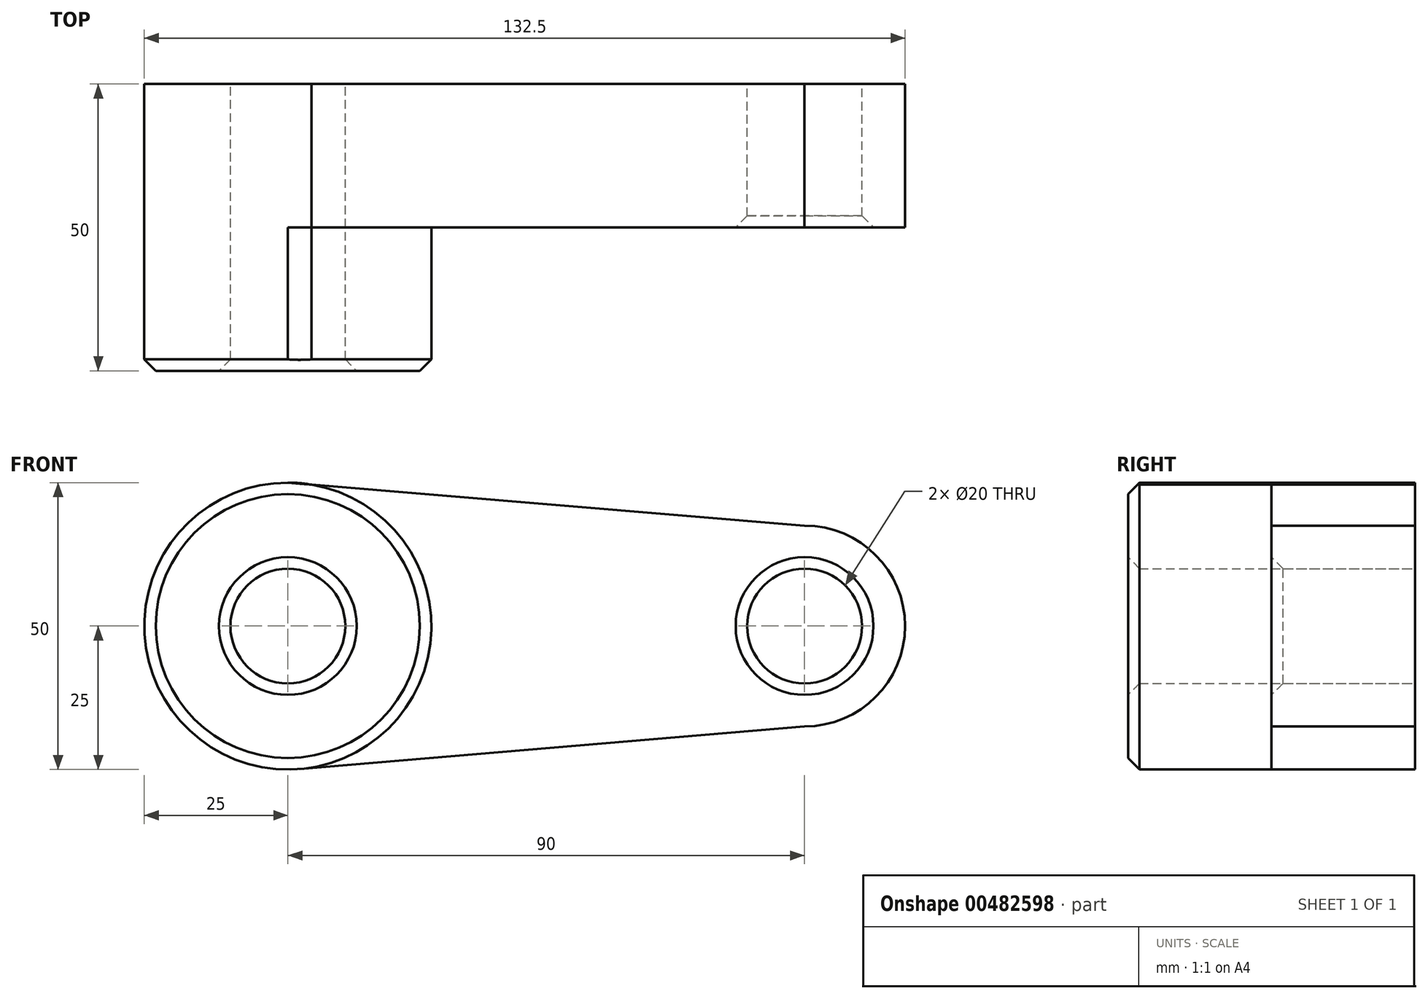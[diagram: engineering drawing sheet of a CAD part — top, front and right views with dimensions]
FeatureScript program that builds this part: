
annotation { "Feature Type Name" : "Feature", "Feature Type Description" : "" }
export const myFeature = defineFeature(function(context is Context, id is Id, definition is map)
    precondition{}
    {
        {
            var Q0;
            Q0=qCreatedBy(makeId("Front.planeOp"),FACE);
            var sketch = newSketch(context, id + "F0", { "sketchPlane" : qUnion([Q0])});
            skCircle(sketch, "E0", {"center": v(0, 0) * mm, "radius": 25 * mm});
            skCircle(sketch, "E1", {"center": v(90, 0) * mm, "radius": 17.5 * mm});
            skCircle(sketch, "E2", {"center": v(0, 0) * mm, "radius": 10 * mm});
            skCircle(sketch, "E3", {"center": v(90, 0) * mm, "radius": 10 * mm});
            skLineSegment(sketch, "E4", {"start": v(0, 25) * mm, "end": v(90, 17.5) * mm});
            skLineSegment(sketch, "E5", {"start": v(90, -17.5) * mm, "end": v(2.1, -24.91) * mm});
            skSolve(sketch);
        }
        {
            var Q0;
            Q0 = qSketchRegion(id + "F0", true);
            extrude(context, id + "F1", {"entities" : qUnion([Q0]), "depth" : 25 * mm});
        }
        {
            var Q0;
            Q0=makeQuery(id+"F0.imprint","IMPRINT",FACE,{"disambiguationData":[TD([[makeQuery(id+"F0.imprint","IMPRINT",EDGE,{"derivedFrom":sQuery(id+"F0.wireOp",EDGE,"E2")}),-1.0]])]});
            extrude(context, id + "F2", {"entities" : qUnion([Q0]), "operationType" : NewBodyOperationType.ADD, "depth" : 50 * mm});
        }
        {
            var Q0;
            Q0=makeQuery(id+"F2.opExtrude","CAP_EDGE",EDGE,{"disambiguationData":[OSD([sQuery(id+"F0.wireOp",EDGE,"E2")])],"isStart":false});
            var Q1;
            Q1=makeQuery(id+"F2.opExtrude","CAP_EDGE",EDGE,{"disambiguationData":[OSD([sQuery(id+"F0.wireOp",EDGE,"E0")])],"isStart":false});
            var Q2;
            Q2=makeQuery(id+"F1.opExtrude","CAP_EDGE",EDGE,{"disambiguationData":[OSD([sQuery(id+"F0.wireOp",EDGE,"E3")])],"isStart":false});
            chamfer(context, id + "F3", {"entities" : qUnion([Q0, Q1, Q2]), "width" : 2 * mm, "tangentPropagation" : true});
        }
    });
